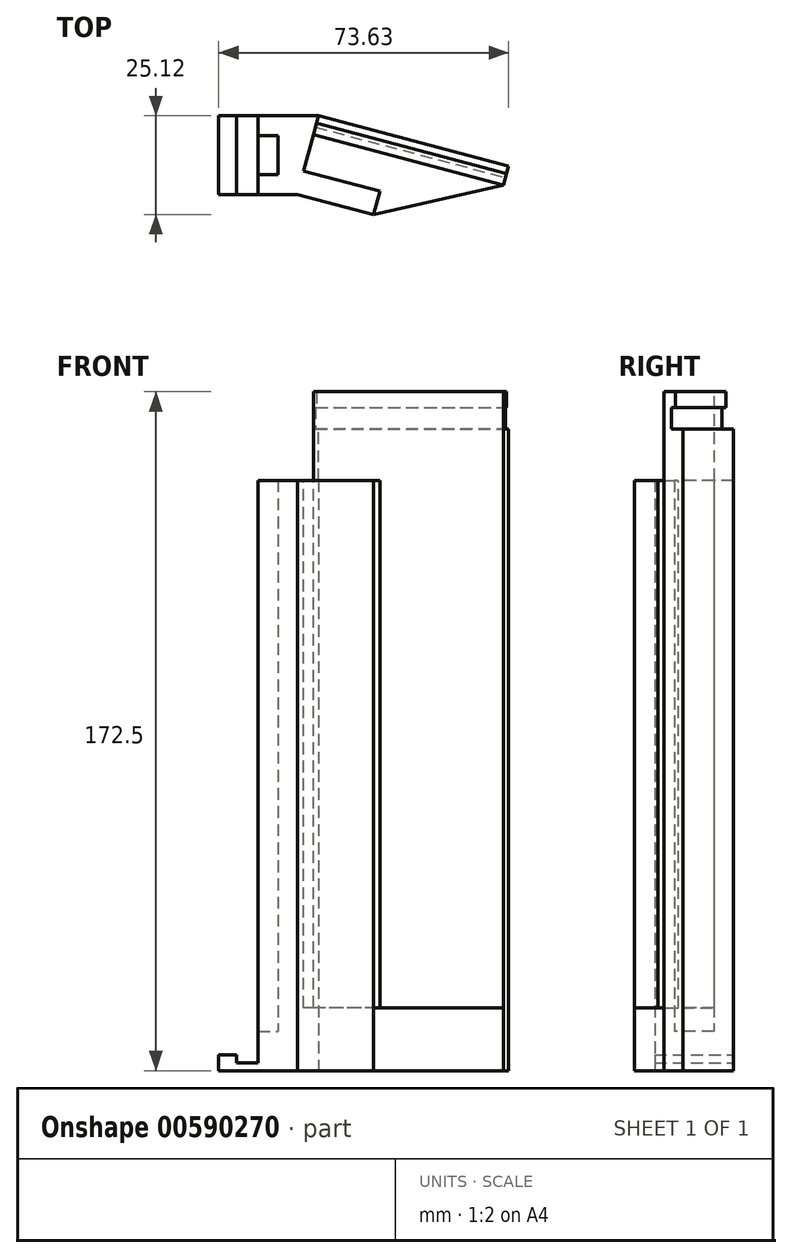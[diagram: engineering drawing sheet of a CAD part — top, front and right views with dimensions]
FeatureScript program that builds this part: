
annotation { "Feature Type Name" : "Feature", "Feature Type Description" : "" }
export const myFeature = defineFeature(function(context is Context, id is Id, definition is map)
    precondition{}
    {
        {
            var Q0;
            Q0=qCreatedBy(makeId("Top.planeOp"),FACE);
            var sketch = newSketch(context, id + "F0", { "sketchPlane" : qUnion([Q0])});
            skLineSegment(sketch, "E0.bottom", {"start": v(0, 0) * mm, "end": v(4.5, 0) * mm});
            skLineSegment(sketch, "E0.top", {"start": v(0, 20) * mm, "end": v(4.5, 20) * mm});
            skLineSegment(sketch, "E0.left", {"start": v(0, 0) * mm, "end": v(0, 20) * mm});
            skLineSegment(sketch, "E0.right", {"start": v(4.5, 0) * mm, "end": v(4.5, 20) * mm});
            skSolve(sketch);
        }
        {
            var Q0;
            Q0 = qSketchRegion(id + "F0", true);
            extrude(context, id + "F1", {"entities" : qUnion([Q0]), "depth" : 4 * mm, "offsetDistance" : 25 * mm});
        }
        {
            var Q0;
            Q0=qCreatedBy(makeId("Top.planeOp"),FACE);
            var sketch = newSketch(context, id + "F2", { "sketchPlane" : qUnion([Q0])});
            skLineSegment(sketch, "E1.bottom", {"start": v(4.5, 0) * mm, "end": v(10, 0) * mm});
            skLineSegment(sketch, "E1.top", {"start": v(4.5, 20) * mm, "end": v(10, 20) * mm});
            skLineSegment(sketch, "E1.left", {"start": v(4.5, 0) * mm, "end": v(4.5, 20) * mm});
            skLineSegment(sketch, "E1.right", {"start": v(10, 0) * mm, "end": v(10, 20) * mm});
            skSolve(sketch);
        }
        {
            var Q0;
            Q0 = qSketchRegion(id + "F2", true);
            extrude(context, id + "F3", {"entities" : qUnion([Q0]), "operationType" : NewBodyOperationType.ADD, "depth" : 2 * mm, "offsetDistance" : 25 * mm});
        }
        {
            var Q0;
            Q0=qCreatedBy(makeId("Top.planeOp"),FACE);
            var sketch = newSketch(context, id + "F4", { "sketchPlane" : qUnion([Q0])});
            skLineSegment(sketch, "E2.bottom", {"start": v(10, 20) * mm, "end": v(15, 20) * mm});
            skLineSegment(sketch, "E2.top", {"start": v(10, 15) * mm, "end": v(15, 15) * mm});
            skLineSegment(sketch, "E2.left", {"start": v(10, 20) * mm, "end": v(10, 15) * mm});
            skLineSegment(sketch, "E2.right", {"start": v(15, 20) * mm, "end": v(15, 15) * mm});
            skLineSegment(sketch, "E3.bottom", {"start": v(10, 0) * mm, "end": v(15, 0) * mm});
            skLineSegment(sketch, "E3.top", {"start": v(10, 5) * mm, "end": v(15, 5) * mm});
            skLineSegment(sketch, "E3.left", {"start": v(10, 0) * mm, "end": v(10, 5) * mm});
            skLineSegment(sketch, "E3.right", {"start": v(15, 0) * mm, "end": v(15, 5) * mm});
            skLineSegment(sketch, "E4.bottom", {"start": v(15, 20) * mm, "end": v(20, 20) * mm});
            skLineSegment(sketch, "E4.top", {"start": v(15, 0) * mm, "end": v(20, 0) * mm});
            skLineSegment(sketch, "E4.left", {"start": v(15, 20) * mm, "end": v(15, 0) * mm});
            skLineSegment(sketch, "E4.right", {"start": v(20, 20) * mm, "end": v(20, 0) * mm});
            skLineSegment(sketch, "E5", {"start": v(20, 20) * mm, "end": v(25.3, 20) * mm});
            skLineSegment(sketch, "E6", {"start": v(25.3, 20) * mm, "end": v(20, 0) * mm});
            skSolve(sketch);
        }
        {
            var Q0;
            Q0 = qSketchRegion(id + "F4", true);
            extrude(context, id + "F5", {"entities" : qUnion([Q0]), "operationType" : NewBodyOperationType.ADD, "depth" : 150 * mm, "offsetDistance" : 25 * mm});
        }
        {
            var Q0;
            Q0=qCreatedBy(makeId("Top.planeOp"),FACE);
            var sketch = newSketch(context, id + "F6", { "sketchPlane" : qUnion([Q0])});
            skLineSegment(sketch, "E7.bottom", {"start": v(10, 15) * mm, "end": v(15, 15) * mm});
            skLineSegment(sketch, "E7.top", {"start": v(10, 5) * mm, "end": v(15, 5) * mm});
            skLineSegment(sketch, "E7.left", {"start": v(10, 15) * mm, "end": v(10, 5) * mm});
            skLineSegment(sketch, "E7.right", {"start": v(15, 15) * mm, "end": v(15, 5) * mm});
            skSolve(sketch);
        }
        {
            var Q0;
            Q0 = qSketchRegion(id + "F6", true);
            extrude(context, id + "F7", {"entities" : qUnion([Q0]), "operationType" : NewBodyOperationType.ADD, "depth" : 10 * mm, "offsetDistance" : 25 * mm});
        }
        {
            var Q0;
            Q0=makeQuery(id+"F5.opExtrude","SWEPT_FACE",FACE,{"disambiguationData":[OSD([sQuery(id+"F4.wireOp",EDGE,"E6")])]});
            var sketch = newSketch(context, id + "F8", { "sketchPlane" : qUnion([Q0])});
            skLineSegment(sketch, "E8.bottom", {"start": v(20.81, 0) * mm, "end": v(11.31, 0) * mm});
            skLineSegment(sketch, "E8.top", {"start": v(20.81, 16) * mm, "end": v(11.31, 16) * mm});
            skLineSegment(sketch, "E8.left", {"start": v(20.81, 0) * mm, "end": v(20.81, 16) * mm});
            skLineSegment(sketch, "E8.right", {"start": v(11.31, 0) * mm, "end": v(11.31, 16) * mm});
            skLineSegment(sketch, "E9.bottom", {"start": v(25.81, 0) * mm, "end": v(20.81, 0) * mm});
            skLineSegment(sketch, "E9.top", {"start": v(25.81, 163) * mm, "end": v(20.81, 163) * mm});
            skLineSegment(sketch, "E9.left", {"start": v(25.81, 0) * mm, "end": v(25.81, 163) * mm});
            skLineSegment(sketch, "E9.right", {"start": v(20.81, 0) * mm, "end": v(20.81, 163) * mm});
            skLineSegment(sketch, "E10.bottom", {"start": v(11.31, 0) * mm, "end": v(5.12, 0) * mm});
            skLineSegment(sketch, "E10.top", {"start": v(11.31, 150) * mm, "end": v(5.12, 150) * mm});
            skLineSegment(sketch, "E10.left", {"start": v(11.31, 0) * mm, "end": v(11.31, 150) * mm});
            skLineSegment(sketch, "E10.right", {"start": v(5.12, 0) * mm, "end": v(5.12, 150) * mm});
            skSolve(sketch);
        }
        {
            var Q0;
            Q0 = qSketchRegion(id + "F8", true);
            extrude(context, id + "F9", {"entities" : qUnion([Q0]), "operationType" : NewBodyOperationType.ADD, "depth" : 20 * mm, "offsetDistance" : 25 * mm});
        }
        {
            var Q0;
            Q0=makeQuery(id+"F9.opExtrude","CAP_FACE",FACE,{"disambiguationData":[OSD([sQuery(id+"F8.wireOp",EDGE,"E8.bottom"),sQuery(id+"F8.wireOp",EDGE,"E8.top"),sQuery(id+"F8.wireOp",EDGE,"E9.bottom"),sQuery(id+"F8.wireOp",EDGE,"E9.top"),sQuery(id+"F8.wireOp",EDGE,"E9.left"),sQuery(id+"F8.wireOp",EDGE,"E9.right"),sQuery(id+"F8.wireOp",EDGE,"E10.bottom"),sQuery(id+"F8.wireOp",EDGE,"E10.top"),sQuery(id+"F8.wireOp",EDGE,"E10.left"),sQuery(id+"F8.wireOp",EDGE,"E10.right")])],"isStart":false});
            var sketch = newSketch(context, id + "F10", { "sketchPlane" : qUnion([Q0])});
            skLineSegment(sketch, "E11.bottom", {"start": v(25.81, 163) * mm, "end": v(20.81, 163) * mm});
            skLineSegment(sketch, "E11.top", {"start": v(25.81, 0) * mm, "end": v(20.81, 0) * mm});
            skLineSegment(sketch, "E11.left", {"start": v(25.81, 163) * mm, "end": v(25.81, 0) * mm});
            skLineSegment(sketch, "E11.right", {"start": v(20.81, 163) * mm, "end": v(20.81, 0) * mm});
            skLineSegment(sketch, "E12.bottom", {"start": v(20.81, 0) * mm, "end": v(5.12, 0) * mm});
            skLineSegment(sketch, "E12.top", {"start": v(20.81, 16) * mm, "end": v(5.12, 16) * mm});
            skLineSegment(sketch, "E12.left", {"start": v(20.81, 0) * mm, "end": v(20.81, 16) * mm});
            skLineSegment(sketch, "E12.right", {"start": v(5.12, 0) * mm, "end": v(5.12, 16) * mm});
            skSolve(sketch);
        }
        {
            var Q0;
            Q0 = qSketchRegion(id + "F10", true);
            extrude(context, id + "F11", {"entities" : qUnion([Q0]), "operationType" : NewBodyOperationType.ADD, "depth" : 30 * mm, "offsetDistance" : 25 * mm});
        }
        {
            var Q0;
            Q0=makeQuery(id+"F11.boolean.opBoolean","MERGE",FACE,{"derivedFrom":[makeQuery(id+"F9.opExtrude","SWEPT_FACE",FACE,{"disambiguationData":[OSD([sQuery(id+"F8.wireOp",EDGE,"E8.top")])]}),makeQuery(id+"F11.opExtrude","SWEPT_FACE",FACE,{"disambiguationData":[OSD([sQuery(id+"F10.wireOp",EDGE,"E12.top")])]})]});
            var sketch = newSketch(context, id + "F12", { "sketchPlane" : qUnion([Q0])});
            skLineSegment(sketch, "E13", {"start": v(39.33, -5.12) * mm, "end": v(68.33, -12.8) * mm});
            skLineSegment(sketch, "E14", {"start": v(68.33, -12.8) * mm, "end": v(72.35, 2.36) * mm});
            skLineSegment(sketch, "E15", {"start": v(72.35, 2.36) * mm, "end": v(39.33, -5.12) * mm});
            skSolve(sketch);
        }
        {
            var Q0;
            Q0 = qSketchRegion(id + "F12", true);
            extrude(context, id + "F13", {"entities" : qUnion([Q0]), "operationType" : NewBodyOperationType.REMOVE, "oppositeDirection" : true, "depth" : 16 * mm, "offsetDistance" : 25 * mm});
        }
        {
            var Q0;
            Q0=makeQuery(id+"F11.boolean.opBoolean","MERGE",FACE,{"derivedFrom":[makeQuery(id+"F9.opExtrude","SWEPT_FACE",FACE,{"disambiguationData":[OSD([sQuery(id+"F8.wireOp",EDGE,"E9.top")])]}),makeQuery(id+"F11.opExtrude","SWEPT_FACE",FACE,{"disambiguationData":[OSD([sQuery(id+"F10.wireOp",EDGE,"E11.bottom")])]})]});
            var sketch = newSketch(context, id + "F14", { "sketchPlane" : qUnion([Q0])});
            skLineSegment(sketch, "E16", {"start": v(24.02, 15.17) * mm, "end": v(24.53, 17.1) * mm});
            skLineSegment(sketch, "E17", {"start": v(24.53, 17.1) * mm, "end": v(72.86, 4.3) * mm});
            skLineSegment(sketch, "E18", {"start": v(72.86, 4.3) * mm, "end": v(72.35, 2.36) * mm});
            skLineSegment(sketch, "E19", {"start": v(72.35, 2.36) * mm, "end": v(24.02, 15.17) * mm});
            skSolve(sketch);
        }
        {
            var Q0;
            Q0 = qSketchRegion(id + "F14", true);
            extrude(context, id + "F15", {"entities" : qUnion([Q0]), "operationType" : NewBodyOperationType.ADD, "depth" : 5.5 * mm, "offsetDistance" : 25 * mm});
        }
        {
            var Q0;
            Q0=makeQuery(id+"F15.opExtrude","CAP_FACE",FACE,{"disambiguationData":[OSD([sQuery(id+"F14.wireOp",EDGE,"E16"),sQuery(id+"F14.wireOp",EDGE,"E17"),sQuery(id+"F14.wireOp",EDGE,"E18"),sQuery(id+"F14.wireOp",EDGE,"E19")])],"isStart":false});
            var sketch = newSketch(context, id + "F16", { "sketchPlane" : qUnion([Q0])});
            skLineSegment(sketch, "E20", {"start": v(24.02, 15.17) * mm, "end": v(24.79, 18.07) * mm});
            skLineSegment(sketch, "E21", {"start": v(24.79, 18.07) * mm, "end": v(73.12, 5.26) * mm});
            skLineSegment(sketch, "E22", {"start": v(72.35, 2.36) * mm, "end": v(24.02, 15.17) * mm});
            skLineSegment(sketch, "E23", {"start": v(73.12, 5.26) * mm, "end": v(72.35, 2.36) * mm});
            skSolve(sketch);
        }
        {
            var Q0;
            Q0 = qSketchRegion(id + "F16", true);
            extrude(context, id + "F17", {"entities" : qUnion([Q0]), "operationType" : NewBodyOperationType.ADD, "depth" : 4 * mm, "offsetDistance" : 25 * mm});
        }
    });
